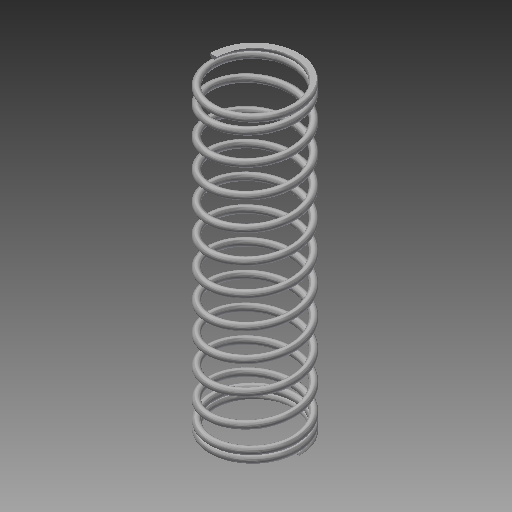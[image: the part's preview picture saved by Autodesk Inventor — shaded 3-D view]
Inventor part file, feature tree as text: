
AUTODESK INVENTOR PART (.ipt)
format: ipt  version: 2019 (Build 230136000, 136)  size: 1,017,344 bytes
history: native  units: in
note: dims shown in document units (in); Inventor stores cm internally (conversion verified against a paired STEP export)
features: other x73, extrude x8, sweep x2, helix x2, plane x1
ambient origin geometry x8: Origin, YZ Plane, XZ Plane, XY Plane, X Axis, Y Axis, Z Axis, Center Point
bodies: Solid1 (feature_tree)
feature tree (86):
  other  "Main Coil Path(Right)"
  other  "Section Work Plane(Right)"
  other  "Start Work Plane(Right)"
  other  "End Work Plane(Right)"
  other  "End Cut Work Plane(Right)"
  other  "Start Cut Work Plane(Right)"
  other  "Plain Ends Cut Work Plane 1(Right)"
  other  "Plain Ends Cut Work Plane 2(Right)"
  sweep  "Main Coil Feature(R)"
  other  "Start Transition Coil 1(Right)"
  other  "Start Transition Coil 2(Right)"
  other  "Start Transition Coil 3(Right)"
  other  "Start Transition Coil 4(Right)"
  other  "Start Ends Coil(Right)"
  extrude  "Start Cut Feature(Right)"  Depth=0.2052in
  other  "End Transition Coil 1(Right)"
  other  "End Transition Coil 2(Right)"
  other  "End Transition Coil 3(Right)"
  other  "End Transition Coil 4(Right)"
  other  "End Coil(Right)"
  extrude  "End Cut Feature(Right)"  Depth=0.1312in
  extrude  "Plain Ends Cut Feature 1(Right)"  Depth=0.05in
  extrude  "Plain Ends Cut Feature 2(Right)"  TaperAngle=0.0deg  [1 undecoded]
  other  "Main Coil Path(Left)"
  other  "Section Work Plane(Left)"
  other  "Start Work Plane(Left)"
  other  "End Work Plane(Left)"
  other  "End Cut Work Plane(Left)"
  other  "Start Cut Work Plane(Left)"
  other  "Plain Ends Cut Work Plane 1(Left)"
  other  "Plain Ends Cut Work Plane 2(Left)"
  sweep  "Main Coil Feature(L)"
  other  "Start Transition Coil 1(Left)"
  other  "Start Transition Coil 2(Left)"
  other  "Start Transition Coil 3(Left)"
  other  "Start Transition Coil 4(Left)"
  other  "Start Ends Coil(Left)"
  extrude  "Start Cut Feature(Left)"  Depth=0.0503in
  other  "End Transition Coil 1(Left)"
  other  "End Transition Coil 2(Left)"
  other  "End Transition Coil 3(Left)"
  other  "End Transition Coil 4(Left)"
  other  "End Coil(Left)"
  extrude  "End Cut Feature(Left)"  Depth=0.3937in
  extrude  "Cut Plain Ends Cut 1(L)"  Depth=0.65in
  extrude  "Cut Plain Ends Cut 2(L)"  Depth=0.05in
  other  "iMate Based Work Plane"
  other  "Preview Center Point"
  other  "Preview X Axis"
  other  "Path Section Sketch(Right)"
  other  "Srf1"
  helix  "Coil Section Sketch(Right)"  [1 undecoded]
  other  "Start Transition Coil Sketch 1(Right)"
  other  "Start Transition Coil Sketch 2(Right)"
  other  "Start Transition Coil Sketch 3(Right)"
  other  "Start Transition Coil Sketch 4(Right)"
  other  "End Transition Coil Sketch 1(Right)"
  other  "End Transition Coil Sketch 2(Right)"
  other  "End Transition Coil Sketch 3(Right)"
  other  "End Transition Coil Sketch 4(Right)"
  other  "Start Ends Skecth(Right)"
  other  "End Coil Skecth(Right)"
  other  "Start Cut Sketch(Right)"
  other  "End Cut Sketch(Right)"
  other  "Plain Ends Cut Sketch 2(Right)"
  other  "Plain Ends Cut Sketch 1(Right)"
  other  "Path Section Sketch(Left)"
  other  "Srf2"
  helix  "Coil Section Sketch(Left)"  [1 undecoded]
  other  "Start Transition Coil Sketch 1(Left)"
  other  "Start Transition Coil Sketch 2(Left)"
  other  "Start Transition Coil Sketch 3(Left)"
  other  "Start Transition Coil Sketch 4(Left)"
  other  "Start Ends Skecth(Left)"
  other  "Start Cut Sketch(Left)"
  other  "End Transition Coil Sketch 1(Left)"
  other  "End Transition Coil Sketch 2(Left)"
  other  "End Transition Coil Sketch 3(Left)"
  other  "End Transition Coil Sketch 4(Left)"
  other  "End Coil Skecth(Left)"
  other  "End Cut Sketch(Left)"
  other  "Plain Ends Cut Sketch 2(Left)"
  other  "Plain Ends Cut Sketch 1(Left)"
  plane  "Work Plane Start Section"
  other  "Basic Curve(Right)"
  other  "Basic Curve(Left)"
note: 3 required parameter values undecoded (feature->parameter linkage not recoverable at this tier; creation-order binding heuristic only, values carry confidence <= 0.55)
